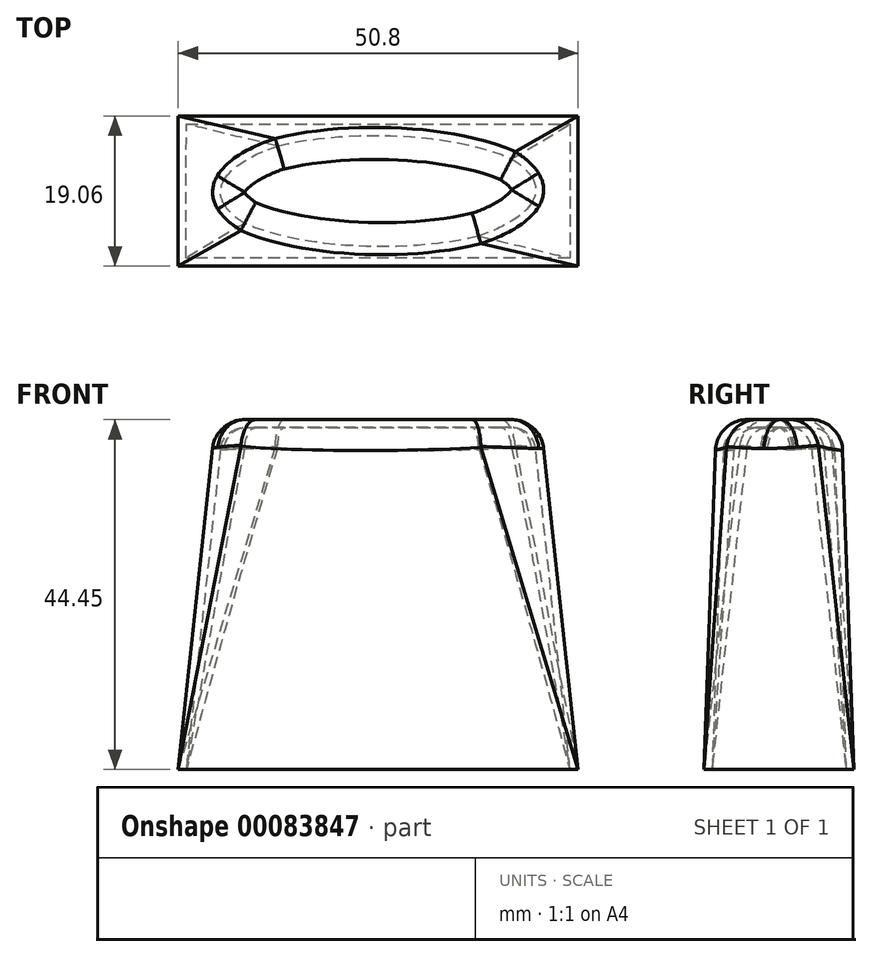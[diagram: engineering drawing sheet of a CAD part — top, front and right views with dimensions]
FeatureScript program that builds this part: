
annotation { "Feature Type Name" : "Feature", "Feature Type Description" : "" }
export const myFeature = defineFeature(function(context is Context, id is Id, definition is map)
    precondition{}
    {
        {
            var Q0;
            Q0=qCreatedBy(makeId("Top.planeOp"),FACE);
            var sketch = newSketch(context, id + "F0", { "sketchPlane" : qUnion([Q0])});
            skLineSegment(sketch, "E0.bottom", {"start": v(25.4, -9.52) * mm, "end": v(-25.4, -9.53) * mm});
            skLineSegment(sketch, "E0.top", {"start": v(25.4, 9.53) * mm, "end": v(-25.4, 9.52) * mm});
            skLineSegment(sketch, "E0.left", {"start": v(25.4, -9.52) * mm, "end": v(25.4, 9.53) * mm});
            skLineSegment(sketch, "E0.right", {"start": v(-25.4, -9.53) * mm, "end": v(-25.4, 9.52) * mm});
            skPoint(sketch, "E0.middle", {"position": v(0, 0) * mm});
            skPoint(sketch, "E1", {"position": v(25.4, 0) * mm});
            skPoint(sketch, "E2", {"position": v(-25.4, 0) * mm});
            skSolve(sketch);
        }
        {
            var Q0;
            Q0=qCreatedBy(makeId("Top.planeOp"),FACE);
            cPlane(context, id + "F1", {"entities" : qUnion([Q0]), "cplaneType" : CPlaneType.OFFSET, "offset" : 44.45 * mm, "width" : 152.4 * mm, "height" : 152.4 * mm});
        }
        {
            var Q0;
            Q0=qCreatedBy(id+"F1.planeOp",FACE);
            var sketch = newSketch(context, id + "F2", { "sketchPlane" : qUnion([Q0])});
            skEllipse(sketch, "E3", {"center": v(0, 0) * mm, "majorRadius": 20.64 * mm, "minorRadius": 7.94 * mm, "majorAxis": v(-1, 0)});
            skPoint(sketch, "E4", {"position": v(-16.78, -4.62) * mm});
            skPoint(sketch, "E5", {"position": v(-16.78, 4.62) * mm});
            skPoint(sketch, "E6", {"position": v(16.78, 4.62) * mm});
            skPoint(sketch, "E7", {"position": v(16.78, -4.62) * mm});
            skPoint(sketch, "E8", {"position": v(20.64, 0) * mm});
            skPoint(sketch, "E9", {"position": v(-20.64, 0) * mm});
            skSolve(sketch);
        }
        {
            var Q0;
            Q0=makeQuery(id+"F2.imprint","IMPRINT",FACE,{"disambiguationData":[TD([[makeQuery(id+"F2.imprint","IMPRINT",EDGE,{"derivedFrom":sQuery(id+"F2.wireOp",EDGE,"E3")}),1.0]])]});
            var Q1;
            Q1=makeQuery(id+"F0.imprint","IMPRINT",FACE,{"disambiguationData":[TD([[makeQuery(id+"F0.imprint","IMPRINT",EDGE,{"derivedFrom":sQuery(id+"F0.wireOp",EDGE,"E0.bottom")}),-1.0]])]});
            var Q2;
            Q2=sQuery(id+"F2.wireOp",VERTEX,"E6");
            var Q3;
            Q3=sQuery(id+"F0.wireOp",VERTEX,"E0.left.end");
            loft(context, id + "F3", {"sheetProfilesArray" : [{ "sheetProfileEntities" : qUnion([Q0]) }, { "sheetProfileEntities" : qUnion([Q1]) }], "matchConnections" : true, "connections" : [{ "connectionEntities" : qUnion([Q2, Q3]), "connectionEdgeQueries" : qUnion([]), "connectionEdgeParameters" : [] }]});
        }
        {
            var Q0;
            Q0=makeQuery(id+"F3.opLoft","CAP_FACE",FACE,{"disambiguationData":[OSD([makeQuery(id+"F2.imprint","IMPRINT",FACE,{"disambiguationData":[TD([[makeQuery(id+"F2.imprint","IMPRINT",EDGE,{"derivedFrom":sQuery(id+"F2.wireOp",EDGE,"E3")}),1.0]])]})])],"isStart":true});
            fillet(context, id + "F4", {"entities" : qUnion([Q0]), "radius" : 4.06 * mm, "tangentPropagation" : true, "allowEdgeOverflow" : false});
        }
        {
            var Q0;
            Q0=makeQuery(id+"F3.opLoft","CAP_FACE",FACE,{"disambiguationData":[OSD([makeQuery(id+"F0.imprint","IMPRINT",FACE,{"disambiguationData":[TD([[makeQuery(id+"F0.imprint","IMPRINT",EDGE,{"derivedFrom":sQuery(id+"F0.wireOp",EDGE,"E0.bottom")}),-1.0]])]})])],"isStart":true});
            shell(context, id + "F5", {"entities" : qUnion([Q0]), "thickness" : 1.02 * mm});
        }
    });
